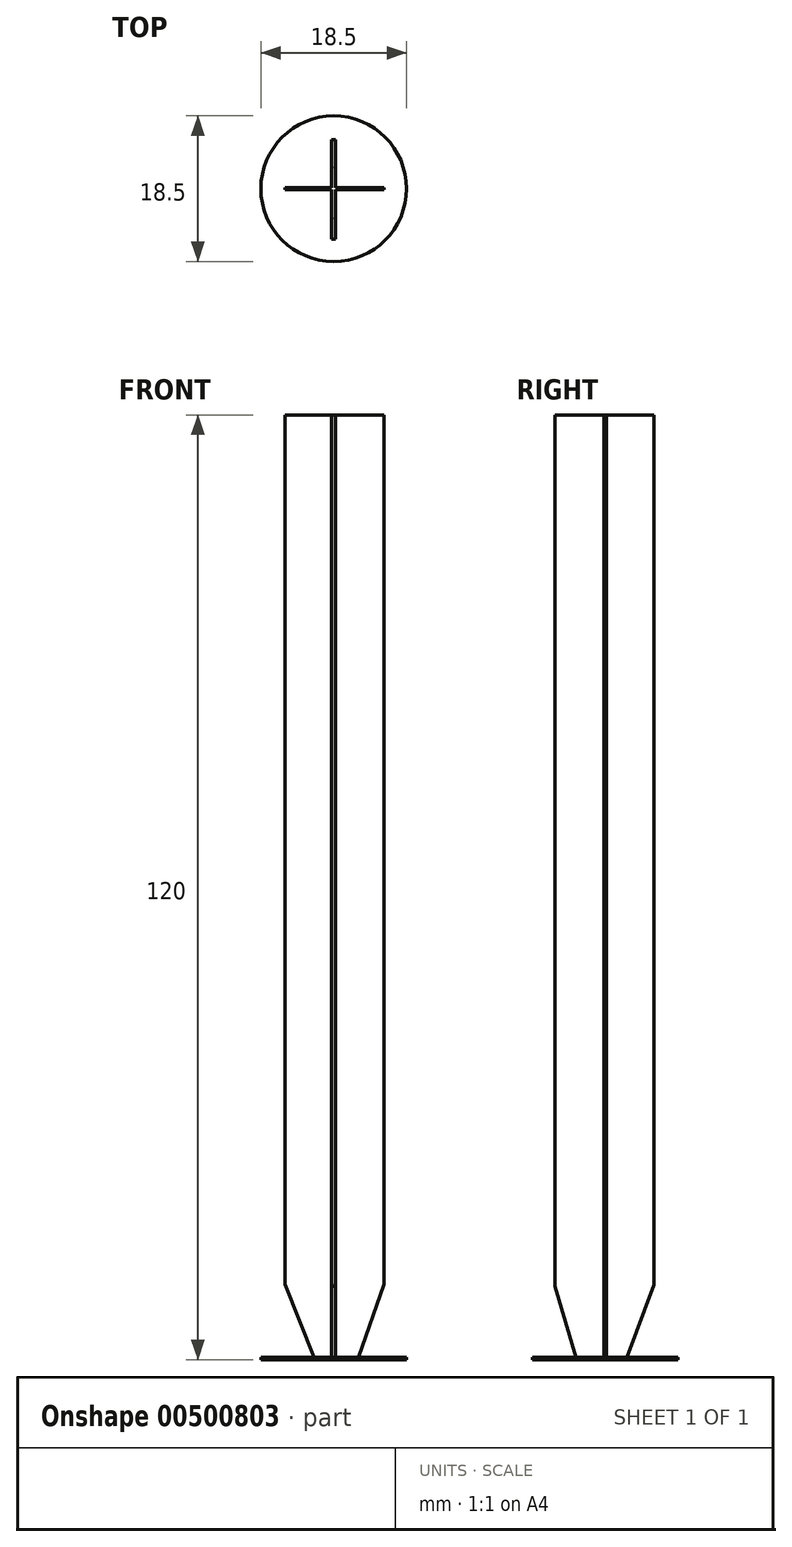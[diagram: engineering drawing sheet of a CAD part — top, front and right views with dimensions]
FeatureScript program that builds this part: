
annotation { "Feature Type Name" : "Feature", "Feature Type Description" : "" }
export const myFeature = defineFeature(function(context is Context, id is Id, definition is map)
    precondition{}
    {
        {
            var Q0;
            Q0=qCreatedBy(makeId("Top.planeOp"),FACE);
            var sketch = newSketch(context, id + "F0", { "sketchPlane" : qUnion([Q0])});
            skCircle(sketch, "E0", {"center": v(0, 0) * mm, "radius": 9.25 * mm});
            skSolve(sketch);
        }
        {
            var Q0;
            Q0=qCreatedBy(makeId("Right.planeOp"),FACE);
            var sketch = newSketch(context, id + "F1", { "sketchPlane" : qUnion([Q0])});
            skLineSegment(sketch, "E1.bottom", {"start": v(-6.4, 0) * mm, "end": v(6.2, 0) * mm});
            skLineSegment(sketch, "E1.top", {"start": v(-6.4, 120) * mm, "end": v(6.2, 120) * mm});
            skLineSegment(sketch, "E1.left", {"start": v(-6.4, 0) * mm, "end": v(-6.4, 120) * mm});
            skLineSegment(sketch, "E1.right", {"start": v(6.2, 0) * mm, "end": v(6.2, 120) * mm});
            skLineSegment(sketch, "E2", {"start": v(-3.67, 0) * mm, "end": v(-6.4, 9.32) * mm});
            skLineSegment(sketch, "E3", {"start": v(-3.67, 0) * mm, "end": v(2.62, 0) * mm});
            skLineSegment(sketch, "E4", {"start": v(2.62, 0) * mm, "end": v(6.2, 9.5) * mm});
            skSolve(sketch);
        }
        {
            var Q0;
            Q0=qCreatedBy(makeId("Front.planeOp"),FACE);
            var sketch = newSketch(context, id + "F2", { "sketchPlane" : qUnion([Q0])});
            skLineSegment(sketch, "E5.bottom", {"start": v(-6.18, 0) * mm, "end": v(6.42, 0) * mm});
            skLineSegment(sketch, "E5.top", {"start": v(-6.18, 120) * mm, "end": v(6.42, 120) * mm});
            skLineSegment(sketch, "E5.left", {"start": v(-6.18, 0) * mm, "end": v(-6.18, 120) * mm});
            skLineSegment(sketch, "E5.right", {"start": v(6.42, 0) * mm, "end": v(6.42, 120) * mm});
            skLineSegment(sketch, "E6", {"start": v(-6.18, 9.58) * mm, "end": v(-2.37, 0) * mm});
            skLineSegment(sketch, "E7", {"start": v(-2.37, 0) * mm, "end": v(3.05, 0) * mm});
            skLineSegment(sketch, "E8", {"start": v(3.05, 0) * mm, "end": v(6.42, 9.58) * mm});
            skSolve(sketch);
        }
        {
            var Q0;
            Q0=makeQuery(id+"F0.imprint","IMPRINT",FACE,{"disambiguationData":[TD([[makeQuery(id+"F0.imprint","IMPRINT",EDGE,{"derivedFrom":sQuery(id+"F0.wireOp",EDGE,"E0")}),1.0]])]});
            var Q1;
            Q1=sQuery(id+"F0.wireOp",EDGE,"E0");
            extrude(context, id + "F3", {"entities" : qUnion([Q0]), "surfaceEntities" : qUnion([Q1]), "depth" : .3 * mm, "offsetDistance" : 25 * mm});
        }
        {
            var Q0;
            {var subQ1=sQuery(id+"F1.wireOp",EDGE,"E1.top");Q0=makeQuery(id+"F1.imprint","IMPRINT",FACE,{"disambiguationData":[TD([[makeQuery(id+"F1.imprint","IMPRINT",EDGE,{"derivedFrom":subQ1}),-1.0]])]});}
            extrude(context, id + "F4", {"entities" : qUnion([Q0]), "depth" : .5 * mm, "offsetDistance" : 25 * mm, "symmetric" : true});
        }
        {
            var Q0;
            {var subQ1=sQuery(id+"F2.wireOp",EDGE,"E5.top");Q0=makeQuery(id+"F2.imprint","IMPRINT",FACE,{"disambiguationData":[TD([[makeQuery(id+"F2.imprint","IMPRINT",EDGE,{"derivedFrom":subQ1}),-1.0]])]});}
            extrude(context, id + "F5", {"entities" : qUnion([Q0]), "operationType" : NewBodyOperationType.ADD, "depth" : .3 * mm, "offsetDistance" : 25 * mm, "symmetric" : true});
        }
    });
